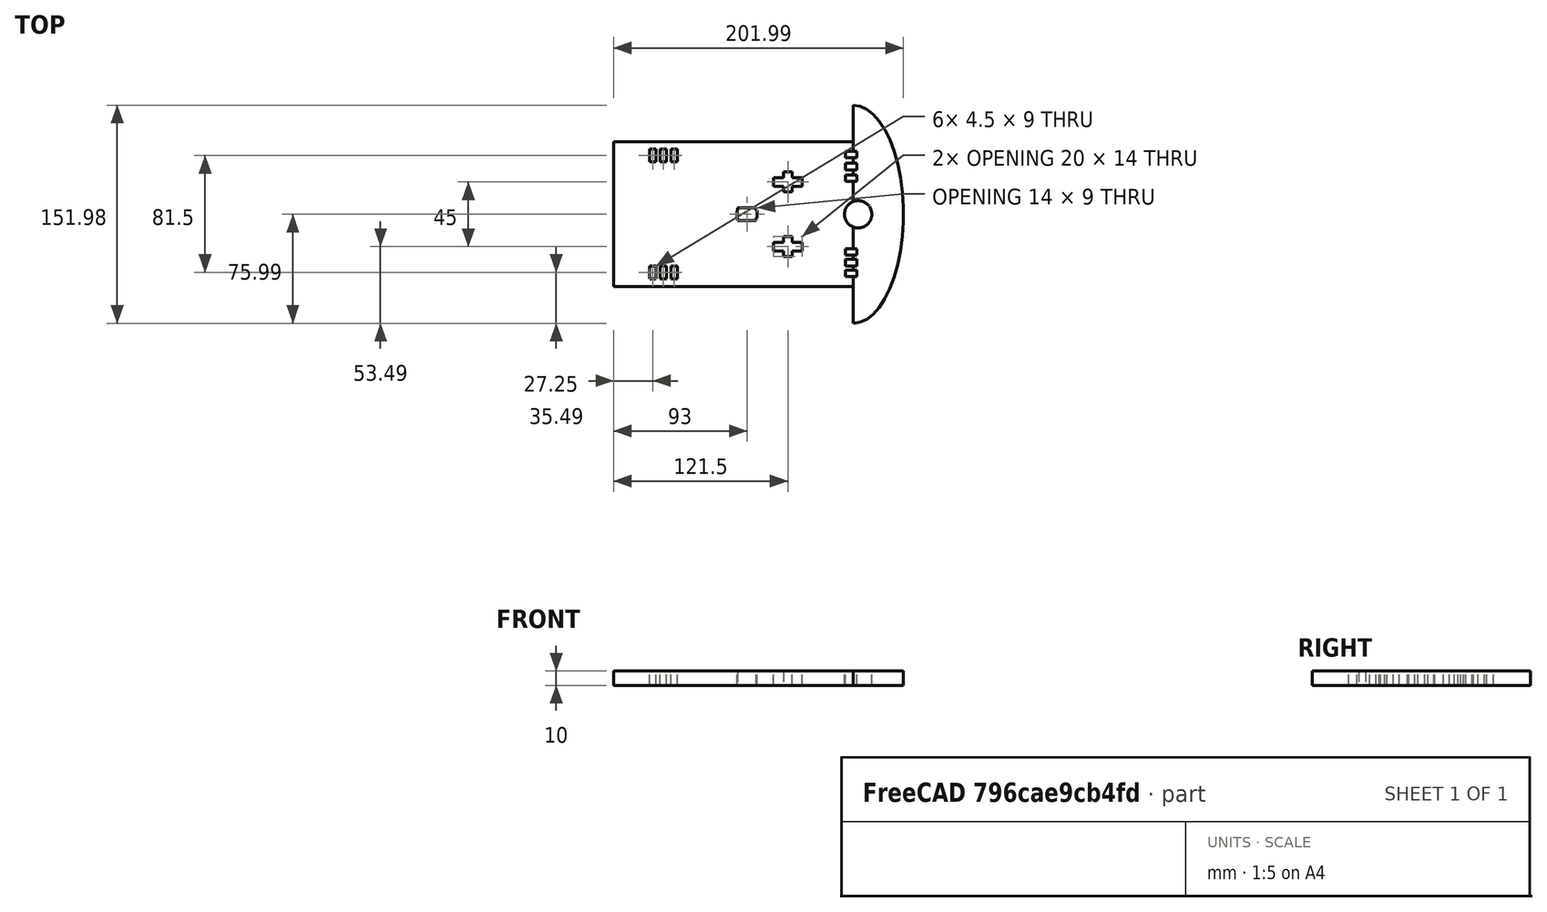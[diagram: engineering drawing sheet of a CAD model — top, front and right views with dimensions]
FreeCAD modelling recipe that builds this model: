
FCSTD DOCUMENT  (FreeCAD 0.18R16131 (Git))
Label: Chassi2
License: All rights reserved
LicenseURL: http://en.wikipedia.org/wiki/All_rights_reserved
objects: Part::Box×20, Part::Fuse×3, Part::Cylinder×1, Sketcher::SketchObject×1, PartDesign::Pad×1, PartDesign::Body×1, Part::MultiCommon×1, Part::FeaturePython×1
note: 30 computed .brp shape members not serialized (recipe doc carries the construction recipe); baked Part::Feature solids carry a one-line shape summary decoded from their .brp

FEATURE [Part::Box] Box  label="Cubo"
  AttacherType = Attacher::AttachEngine3D
  Height = 10
  Length = 167
  Width = 101
FEATURE [Part::Box] Box001  label="Cubo001"
  AttacherType = Attacher::AttachEngine3D
  Height = 10
  Length = 35
  Placement = pos=(167,-25.5,0) rot=(0,0,1;0rad)
  Width = 152
FEATURE [Part::Cylinder] Cylinder  label="Cilindro"
  Angle = 360
  AttacherType = Attacher::AttachEngine3D
  Height = 10
  Placement = pos=(170.5,50.5,0) rot=(0,0,1;0rad)
  Radius = 9.5
FEATURE [Part::Box] Box002  label="Cubo002"
  AttacherType = Attacher::AttachEngine3D
  Height = 10
  Length = 14
  Placement = pos=(0,2,0) rot=(0,0,1;0rad)
  Width = 5
FEATURE [Part::Box] Box003  label="Cubo003"
  AttacherType = Attacher::AttachEngine3D
  Height = 10
  Length = 13
  Placement = pos=(0.5,0,0) rot=(0,0,1;0rad)
  Width = 9
FEATURE [Part::Fuse] Fusion
  Base = -> Box002
  Placement = pos=(86,46,0) rot=(0,0,1;0rad)
  Tool = -> Box003
FEATURE [Sketcher::SketchObject] Sketch
  MapMode = 5
  Support = -> [XY_Plane]
  sketch-geometry (1):
    g0: Ellipse CenterX=0 CenterY=0 CenterZ=0 NormalX=0 NormalY=0 NormalZ=1 MajorRadius=75.9942 MinorRadius=34.993 AngleXU=1.57073
  constraints (1):
    c: Coincident(g0,g-1)
FEATURE [PartDesign::Pad] Pad
  Length = 10
  Length2 = 100
  Profile = -> Sketch
  Type = 0
FEATURE [PartDesign::Body] Body
  Group = -> [Sketch,Pad]
  Origin = -> Origin
  Placement = pos=(167,50.5,0) rot=(0,0,1;0rad)
  Tip = -> Pad
FEATURE [Part::MultiCommon] Common
  Shapes = -> [Body,Box001]
FEATURE [Part::Box] Box004  label="Cubo004"
  AttacherType = Attacher::AttachEngine3D
  Height = 10
  Length = 20
  Placement = pos=(0,4,0) rot=(0,0,1;0rad)
  Width = 6
FEATURE [Part::Box] Box005  label="Cubo005"
  AttacherType = Attacher::AttachEngine3D
  Height = 10
  Length = 6
  Placement = pos=(7,0,0) rot=(0,0,1;0rad)
  Width = 14
FEATURE [Part::Fuse] Fusion001
  Base = -> Box004
  Placement = pos=(111.5,66,0) rot=(0,0,1;0rad)
  Tool = -> Box005
FEATURE [Part::Box] Box006  label="Cubo006"
  AttacherType = Attacher::AttachEngine3D
  Height = 10
  Length = 6
  Placement = pos=(7,0,0) rot=(0,0,1;0rad)
  Width = 14
FEATURE [Part::Box] Box007  label="Cubo007"
  AttacherType = Attacher::AttachEngine3D
  Height = 10
  Length = 20
  Placement = pos=(0,4,0) rot=(0,0,1;0rad)
  Width = 6
FEATURE [Part::Fuse] Fusion002
  Base = -> Box007
  Placement = pos=(111.5,21,0) rot=(0,0,1;0rad)
  Tool = -> Box006
FEATURE [Part::Box] Box008  label="Cubo008"
  AttacherType = Attacher::AttachEngine3D
  Height = 10
  Length = 8
  Placement = pos=(161.5,7,0) rot=(0,0,1;0rad)
  Width = 4.5
FEATURE [Part::Box] Box009  label="Cubo009"
  AttacherType = Attacher::AttachEngine3D
  Height = 10
  Length = 8
  Placement = pos=(161.5,14.5,0) rot=(0,0,1;0rad)
  Width = 4.5
FEATURE [Part::Box] Box010  label="Cubo010"
  AttacherType = Attacher::AttachEngine3D
  Height = 10
  Length = 8
  Placement = pos=(161.5,22,0) rot=(0,0,1;0rad)
  Width = 4.5
FEATURE [Part::Box] Box011  label="Cubo011"
  AttacherType = Attacher::AttachEngine3D
  Height = 10
  Length = 8
  Placement = pos=(161.5,90,0) rot=(0,0,1;0rad)
  Width = 4.5
FEATURE [Part::Box] Box012  label="Cubo012"
  AttacherType = Attacher::AttachEngine3D
  Height = 10
  Length = 8
  Placement = pos=(161.5,81.5,0) rot=(0,0,1;0rad)
  Width = 4.5
FEATURE [Part::Box] Box013  label="Cubo013"
  AttacherType = Attacher::AttachEngine3D
  Height = 10
  Length = 8
  Placement = pos=(161.5,73.5,0) rot=(0,0,1;0rad)
  Width = 4.5
FEATURE [Part::Box] Box014  label="Cubo014"
  AttacherType = Attacher::AttachEngine3D
  Height = 10
  Length = 4.5
  Placement = pos=(25,5.5,0) rot=(0,0,1;0rad)
  Width = 9
FEATURE [Part::Box] Box015  label="Cubo015"
  AttacherType = Attacher::AttachEngine3D
  Height = 10
  Length = 4.5
  Placement = pos=(32.5,5.5,0) rot=(0,0,1;0rad)
  Width = 9
FEATURE [Part::Box] Box016  label="Cubo016"
  AttacherType = Attacher::AttachEngine3D
  Height = 10
  Length = 4.5
  Placement = pos=(40,5.5,0) rot=(0,0,1;0rad)
  Width = 9
FEATURE [Part::Box] Box017  label="Cubo017"
  AttacherType = Attacher::AttachEngine3D
  Height = 10
  Length = 4.5
  Placement = pos=(25,87,0) rot=(0,0,1;0rad)
  Width = 9
FEATURE [Part::Box] Box018  label="Cubo018"
  AttacherType = Attacher::AttachEngine3D
  Height = 10
  Length = 4.5
  Placement = pos=(32.5,87,0) rot=(0,0,1;0rad)
  Width = 9
FEATURE [Part::Box] Box019  label="Cubo019"
  AttacherType = Attacher::AttachEngine3D
  Height = 10
  Length = 4.5
  Placement = pos=(40,87,0) rot=(0,0,1;0rad)
  Width = 9
FEATURE [Part::FeaturePython] XOR  # WARN: FeaturePython — macro-defined, semantics opaque (R4)
  Objects = -> [Box008,Cylinder,Box,Box012,Box009,Box010,Box011,Box013,Box014,Box015,Box016,Box017,Fusion,Common,Fusion001,Fusion002,Box018,Box019]
  Tolerance = 0
